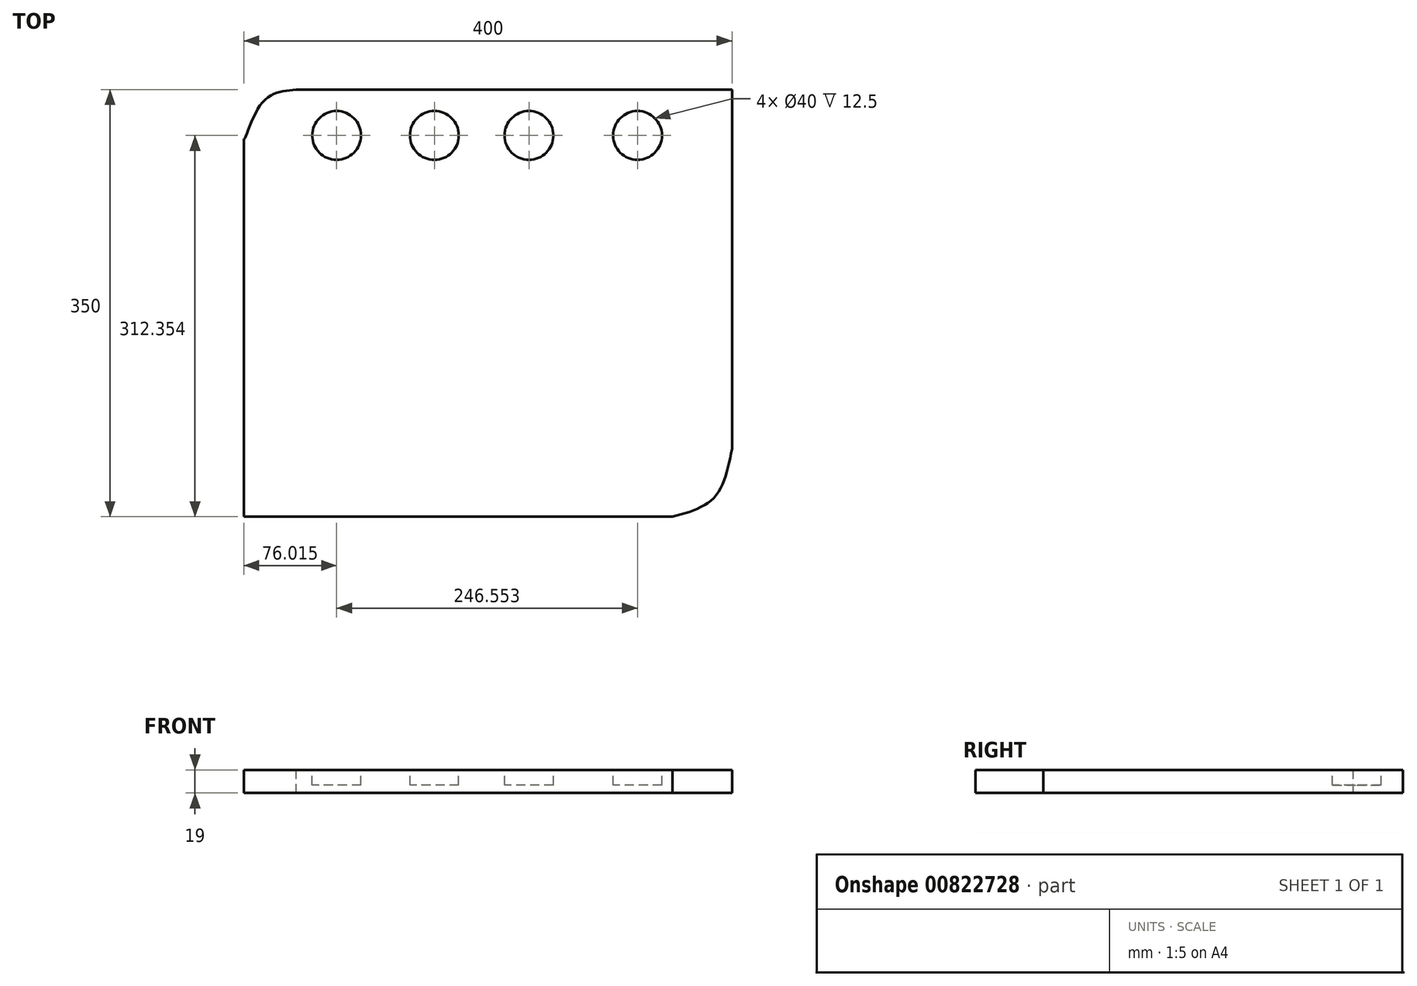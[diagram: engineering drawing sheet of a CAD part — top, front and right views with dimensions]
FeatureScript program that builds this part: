
annotation { "Feature Type Name" : "Feature", "Feature Type Description" : "" }
export const myFeature = defineFeature(function(context is Context, id is Id, definition is map)
    precondition{}
    {
        {
            var Q0;
            Q0=qCreatedBy(makeId("Top.planeOp"),FACE);
            var sketch = newSketch(context, id + "F0", { "sketchPlane" : qUnion([Q0])});
            skLineSegment(sketch, "E0.bottom", {"start": v(-200, -175) * mm, "end": v(200, -175) * mm});
            skLineSegment(sketch, "E0.top", {"start": v(-200, 175) * mm, "end": v(200, 175) * mm});
            skLineSegment(sketch, "E0.left", {"start": v(-200, -175) * mm, "end": v(-200, 175) * mm});
            skLineSegment(sketch, "E0.right", {"start": v(200, -175) * mm, "end": v(200, 175) * mm});
            skPoint(sketch, "E0.middle", {"position": v(0, 0) * mm});
            skSolve(sketch);
        }
        {
            var Q0;
            Q0 = qSketchRegion(id + "F0", true);
            extrude(context, id + "F1", {"entities" : qUnion([Q0]), "depth" : 19 * mm, "offsetDistance" : 25 * mm});
        }
        {
            var Q0;
            Q0=makeQuery(id+"F1.opExtrude","CAP_FACE",FACE,{"disambiguationData":[OSD([sQuery(id+"F0.wireOp",EDGE,"E0.bottom"),sQuery(id+"F0.wireOp",EDGE,"E0.top"),sQuery(id+"F0.wireOp",EDGE,"E0.left"),sQuery(id+"F0.wireOp",EDGE,"E0.right")])],"isStart":false});
            var sketch = newSketch(context, id + "F2", { "sketchPlane" : qUnion([Q0])});
            skFitSpline(sketch, "E1", {"points": [v(-157.2, 175) * mm, v(-185.28, 163.8) * mm, v(-200, 134.53) * mm, v(-200, 137.35) * mm], "startDerivative": vector(-69.42, -9.85) * mm, "endDerivative": vector(2.59, -11) * mm});
            skFitSpline(sketch, "E2", {"points": [v(153.87, -175) * mm, v(181.65, -156.75) * mm, v(200, -126.87) * mm, v(200, -129.5) * mm], "startDerivative": vector(65.96, 25.72) * mm, "endDerivative": vector(-4.22, -32.87) * mm});
            skCircle(sketch, "E3", {"center": v(122.57, 137.35) * mm, "radius": 20 * mm});
            skCircle(sketch, "E4", {"center": v(33.6, 137.35) * mm, "radius": 20 * mm});
            skCircle(sketch, "E5", {"center": v(-43.9, 137.35) * mm, "radius": 20 * mm});
            skCircle(sketch, "E6", {"center": v(-123.99, 137.35) * mm, "radius": 20 * mm});
            skSolve(sketch);
        }
        {
            var Q0;
            Q0=makeQuery(id+"F1.opExtrude","CAP_FACE",FACE,{"disambiguationData":[OSD([sQuery(id+"F0.wireOp",EDGE,"E0.bottom"),sQuery(id+"F0.wireOp",EDGE,"E0.top"),sQuery(id+"F0.wireOp",EDGE,"E0.left"),sQuery(id+"F0.wireOp",EDGE,"E0.right")])],"isStart":false});
            var sketch = newSketch(context, id + "F3", { "sketchPlane" : qUnion([Q0])});
            skFitSpline(sketch, "E7", {"points": [v(151.25, -175) * mm, v(185.32, -159.37) * mm, v(200, -119.53) * mm], "startDerivative": vector(80.48, 21.35) * mm, "endDerivative": vector(17.67, 88.89) * mm});
            skSolve(sketch);
        }
        {
            var Q0;
            {var subQ0=sQuery(id+"F3.wireOp",EDGE,"E7");Q0=makeQuery(id+"F3.imprint","IMPRINT",FACE,{"disambiguationData":[TD([[makeQuery(id+"F3.imprint","IMPRINT",EDGE,{"derivedFrom":subQ0}),-1.0]])]});}
            extrude(context, id + "F4", {"entities" : qUnion([Q0]), "operationType" : NewBodyOperationType.REMOVE, "endBound" : BoundingType.THROUGH_ALL, "oppositeDirection" : true, "depth" : 25 * mm, "offsetDistance" : 25 * mm});
        }
        {
            var Q0;
            Q0 = qSketchRegion(id + "F2", true);
            extrude(context, id + "F5", {"entities" : qUnion([Q0]), "operationType" : NewBodyOperationType.REMOVE, "endBound" : BoundingType.SYMMETRIC, "oppositeDirection" : true, "depth" : 25 * mm, "offsetDistance" : 25 * mm});
        }
        {
            var Q0;
            {var subQ0=sQuery(id+"F2.wireOp",EDGE,"E1");var subQ1=makeQuery(id+"F1.opExtrude","CAP_EDGE",EDGE,{"disambiguationData":[OSD([sQuery(id+"F0.wireOp",EDGE,"E0.top")])],"isStart":false});var subQ2=makeQuery(id+"F2.imprint","INTERSECT",VERTEX,{"derivedFrom":[subQ1,subQ0]});Q0=makeQuery(id+"F2.imprint","IMPRINT",FACE,{"disambiguationData":[TD([[makeQuery(id+"F2.imprint","IMPRINT",EDGE,{"disambiguationData":[TD([[subQ2,-1.0]])],"derivedFrom":subQ0}),-1.0]])]});}
            extrude(context, id + "F6", {"entities" : qUnion([Q0]), "operationType" : NewBodyOperationType.REMOVE, "endBound" : BoundingType.THROUGH_ALL, "oppositeDirection" : true, "depth" : 25 * mm, "offsetDistance" : 25 * mm});
        }
    });
